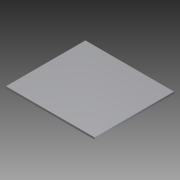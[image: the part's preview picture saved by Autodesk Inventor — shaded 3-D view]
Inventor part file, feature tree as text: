
AUTODESK INVENTOR PART (.ipt)
format: ipt  version: 2012 (Build 160160000, 160)  size: 68,608 bytes
history: native  units: mm
features: extrude x1, sketch x1
ambient origin geometry x8: Origin, YZ Plane, XZ Plane, XY Plane, X Axis, Y Axis, Z Axis, Center Point
bodies: Solid1 (feature_tree)
feature tree (2):
  extrude  "Extrusion1"  Depth=215.0mm
  sketch  "Sketch1"  dims[d0=240.0mm d1=215.0mm d2=5.0mm d3=0.0mm]
